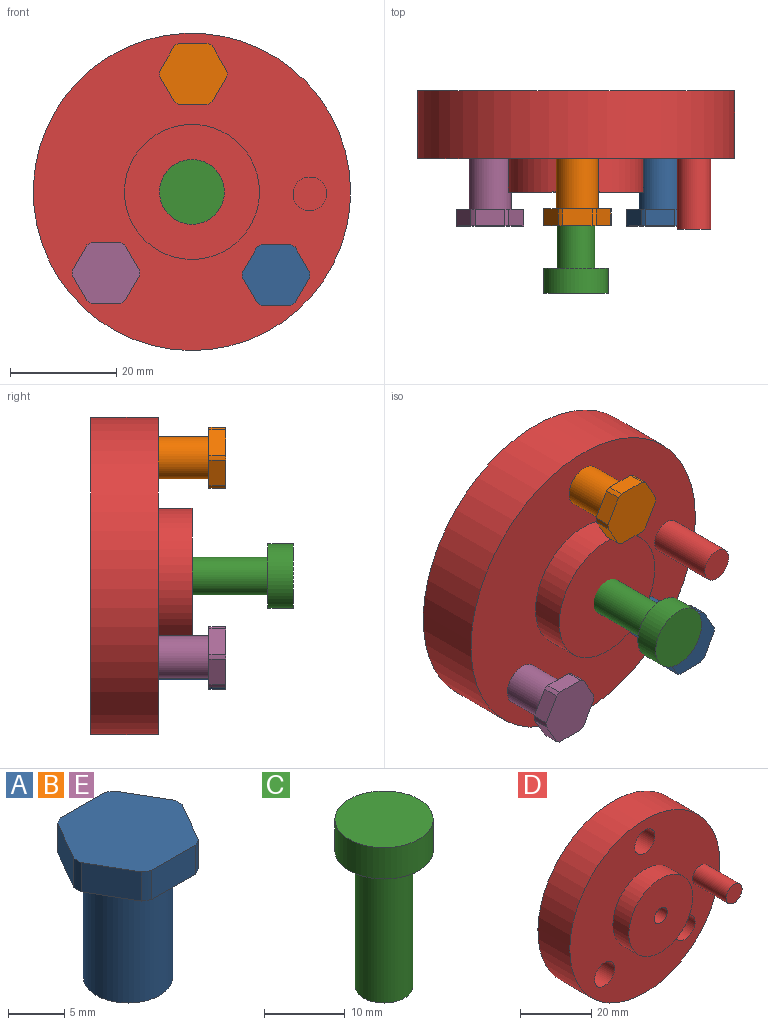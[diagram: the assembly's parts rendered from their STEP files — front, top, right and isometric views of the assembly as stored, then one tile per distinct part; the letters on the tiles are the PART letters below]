
ASSEMBLY  parts=5 mates=4
PART A: 16 faces, bbox 12.7x11.4x15.9 mm
  f0: plane 12.7x11.43mm, normal (0,0,-1), area 63mm2, adj f1,f2,f3,f4,f5,f6,f7,f10
  f1: cylinder r=6.35mm len=3.18mm, axis (0,0,1), area 2.9mm2, adj f0,f8,f10,f15
  f2: cylinder r=6.35mm len=3.18mm, axis (0,0,1), area 2.9mm2, adj f0,f8,f13,f14
  f3: cylinder r=6.35mm len=3.18mm, axis (0,0,1), area 2.9mm2, adj f0,f8,f13,f15
  f4: cylinder r=6.35mm len=3.18mm, axis (0,0,1), area 2.9mm2, adj f0,f8,f12,f14
  f5: cylinder r=6.35mm len=3.18mm, axis (0,0,1), area 2.9mm2, adj f0,f8,f11,f12
  f6: cylinder r=3.97mm len=12.7mm, axis (0,0,1), area 316.7mm2, adj f0,f9
  f7: cylinder r=6.35mm len=3.18mm, axis (0,0,1), area 2.9mm2, adj f0,f8,f10,f11
  f8: plane 12.7x11.43mm, normal (0,0,1), area 112.5mm2, adj f1,f2,f3,f4,f5,f7,f10,f11
  f9: plane 7.94x7.94mm, normal (0,0,-1), area 49.5mm2, adj f6
  f10: plane 4.79x3.18mm, normal (-0.87,0.5,0), area 17.6mm2, adj f0,f1,f7,f8
  f11: plane 5.54x3.18mm, normal (0,1,0), area 17.6mm2, adj f0,f5,f7,f8
  f12: plane 4.79x3.18mm, normal (0.87,0.5,0), area 17.6mm2, adj f0,f4,f5,f8
  f13: plane 5.54x3.18mm, normal (0,-1,0), area 17.6mm2, adj f0,f2,f3,f8
  f14: plane 4.79x3.18mm, normal (0.87,-0.5,0), area 17.6mm2, adj f0,f2,f4,f8
  f15: plane 4.79x3.18mm, normal (-0.87,-0.5,0), area 17.6mm2, adj f0,f1,f3,f8
PART B: same geometry as A
PART C: 5 faces, bbox 12.2x12.2x25.4 mm
  f0: cylinder r=3.56mm len=20.64mm, axis (0,0,1), area 461.1mm2, adj f1,f4
  f1: plane 12.19x12.19mm, normal (0,0,-1), area 77mm2, adj f0,f2
  f2: cylinder r=6.1mm len=12.19mm, axis (0,0,1), area 182.4mm2, adj f1,f3
  f3: plane 12.19x12.19mm, normal (0,0,1), area 116.7mm2, adj f2
  f4: plane 7.11x7.11mm, normal (0,0,-1), area 39.7mm2, adj f0
PART D: 11 faces, bbox 59.7x26x59.7 mm
  f0: cylinder r=4mm len=12.7mm, axis (0,1,0), area 319.2mm2, adj f4,f5
  f1: cylinder r=4mm len=12.7mm, axis (0,1,0), area 319.2mm2, adj f4,f5
  f2: cylinder r=4mm len=12.7mm, axis (0,1,0), area 319.2mm2, adj f4,f5
  f3: cylinder r=29.84mm len=59.69mm, axis (0,1,0), area 2381.5mm2, adj f4,f5
  f4: plane 59.69x59.69mm, normal (0,-1,0), area 2109.1mm2, adj f0,f1,f2,f3,f6,f8
  f5: plane 59.69x59.69mm, normal (0,1,0), area 2627.2mm2, adj f0,f1,f2,f3,f10
  f6: cylinder r=3.17mm len=13.34mm, axis (0,1,0), area 266mm2, adj f4,f7
  f7: plane 6.35x6.35mm, normal (0,-1,0), area 31.7mm2, adj f6
  f8: cylinder r=12.7mm len=25.4mm, axis (0,1,0), area 506.7mm2, adj f4,f9
  f9: plane 25.4x25.4mm, normal (0,-1,0), area 486.4mm2, adj f8,f10
  f10: cylinder r=2.54mm len=19.05mm, axis (0,-1,0), area 304mm2, adj f5,f9
PART E: same geometry as A
PLACE A rot(axis=(1,0,0),90deg) t=(-4.25,-33.26,-12.44)mm
PLACE B rot(axis=(1,0,0),90deg) t=(-19.83,-33.26,25.39)mm
PLACE C rot(axis=(1,0.01,-0.01),90deg) t=(-20.08,-45.96,3.17)mm
PLACE D rot(axis=(0,1,0),0.7deg) t=(-20.08,-7.86,3.17)mm
PLACE E rot(axis=(1,0,0),90deg) t=(-36.25,-33.26,-12.07)mm
MATE cylindrical A.f1 <-> D.f2  axis (0,-1,0) through (-4.25,-30.09,-12.44)mm
MATE cylindrical D.f0 <-> B.f1  axis (0,-1,0) through (-19.83,-20.56,25.39)mm
MATE cylindrical C.f0 <-> D.f8  axis (0,-1,0) through (-20.08,-45.96,3.17)mm
MATE cylindrical E.f1 <-> D.f1  axis (0,-1,0) through (-36.25,-30.09,-12.07)mm
